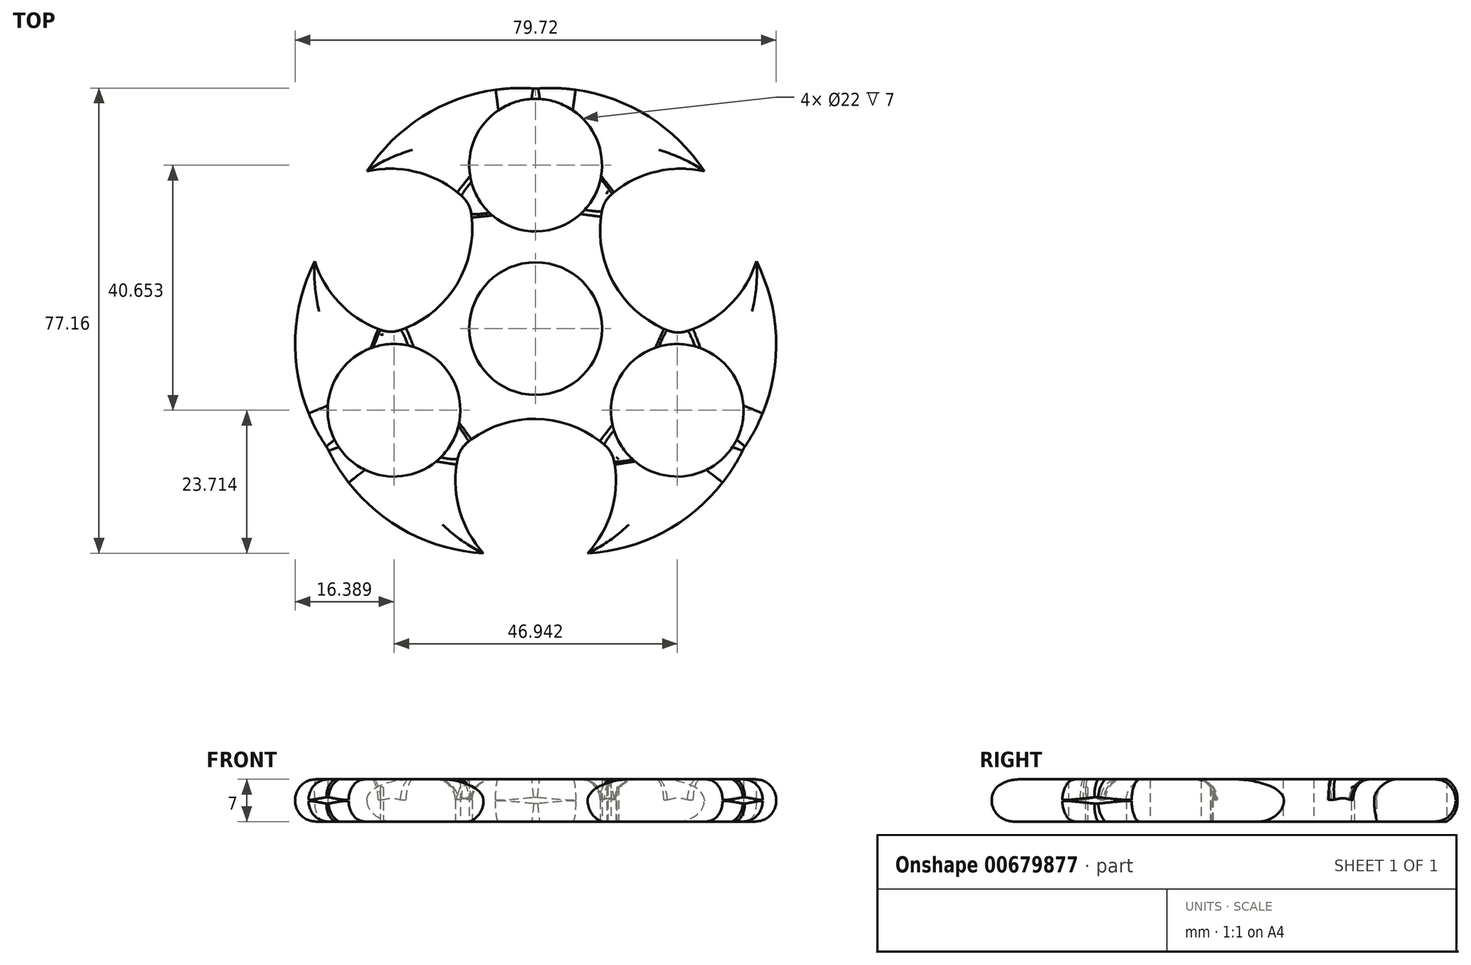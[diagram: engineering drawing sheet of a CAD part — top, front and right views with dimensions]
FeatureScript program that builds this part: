
annotation { "Feature Type Name" : "Feature", "Feature Type Description" : "" }
export const myFeature = defineFeature(function(context is Context, id is Id, definition is map)
    precondition{}
    {
        {
            var Q0;
            Q0=qCreatedBy(makeId("Top.planeOp"),FACE);
            var sketch = newSketch(context, id + "F0", { "sketchPlane" : qUnion([Q0])});
            skCircle(sketch, "E0", {"center": v(0, 40.4) * mm, "radius": 11 * mm});
            skCircle(sketch, "E1.1.0", {"center": v(-23.47, -0.25) * mm, "radius": 11 * mm});
            skCircle(sketch, "E1.2.0", {"center": v(23.47, -0.25) * mm, "radius": 11 * mm});
            skPoint(sketch, "E1.center", {"position": v(0, 13.3) * mm});
            skCircle(sketch, "E2", {"center": v(0, 13.3) * mm, "radius": 11 * mm});
            skCircle(sketch, "E3", {"center": v(0, 40.4) * mm, "radius": 12.7 * mm});
            skCircle(sketch, "E4.1.0", {"center": v(-23.47, -0.25) * mm, "radius": 12.7 * mm});
            skCircle(sketch, "E4.2.0", {"center": v(23.47, -0.25) * mm, "radius": 12.7 * mm});
            skArc(sketch, "E5", {"start": v(11.95, 36.1) * mm, "mid": v(12.48, 21.73) * mm, "end": v(23.47, 12.45) * mm});
            skArc(sketch, "E6.1.0", {"start": v(-25.72, 12.25) * mm, "mid": v(-13.54, 19.9) * mm, "end": v(-11, 34.06) * mm});
            skArc(sketch, "E6.2.0", {"start": v(13.77, -8.44) * mm, "mid": v(1.06, -1.72) * mm, "end": v(-12.47, -6.6) * mm});
            skArc(sketch, "E7", {"start": v(-11, 34.06) * mm, "mid": v(-18.76, 39) * mm, "end": v(-27.95, 39.41) * mm});
            skArc(sketch, "E8.1.0", {"start": v(-12.47, -6.6) * mm, "mid": v(-12.88, -15.8) * mm, "end": v(-8.63, -23.96) * mm});
            skArc(sketch, "E8.2.0", {"start": v(23.47, 12.45) * mm, "mid": v(31.64, 16.7) * mm, "end": v(36.59, 24.46) * mm});
            skArc(sketch, "E9", {"start": v(-35.8, -3.33) * mm, "mid": v(-25.37, -17.8) * mm, "end": v(-8.63, -23.96) * mm});
            skArc(sketch, "E10.1.0", {"start": v(32.3, -9.37) * mm, "mid": v(39.62, 6.89) * mm, "end": v(36.59, 24.46) * mm});
            skArc(sketch, "E10.2.0", {"start": v(3.49, 52.62) * mm, "mid": v(-14.25, 50.82) * mm, "end": v(-27.95, 39.41) * mm});
            skArc(sketch, "E11.MirrorCS", {"start": v(-3.49, 52.62) * mm, "mid": v(14.25, 50.82) * mm, "end": v(27.95, 39.41) * mm});
            skArc(sketch, "E12.MirrorCS", {"start": v(11, 34.06) * mm, "mid": v(18.76, 39) * mm, "end": v(27.95, 39.41) * mm});
            skArc(sketch, "E13.1.0", {"start": v(-23.47, 12.45) * mm, "mid": v(-31.64, 16.7) * mm, "end": v(-36.59, 24.46) * mm});
            skArc(sketch, "E13.1.1", {"start": v(-32.3, -9.37) * mm, "mid": v(-39.62, 6.89) * mm, "end": v(-36.59, 24.46) * mm});
            skArc(sketch, "E13.2.0", {"start": v(12.47, -6.6) * mm, "mid": v(12.88, -15.8) * mm, "end": v(8.63, -23.96) * mm});
            skArc(sketch, "E13.2.1", {"start": v(35.8, -3.33) * mm, "mid": v(25.37, -17.8) * mm, "end": v(8.63, -23.96) * mm});
            skSolve(sketch);
        }
        {
            var Q0;
            Q0=qSketchRegion(id+"F0",true);
            extrude(context, id + "F1", {"entities" : qUnion([Q0]), "depth" : 7 * mm, "offsetDistance" : 25.4 * mm});
        }
        {
            var Q0;
            Q0=makeQuery(id+"F1.opExtrude","SWEPT_EDGE",EDGE,{"disambiguationData":[OSD([sQuery(id+"F0.wireOp",EDGE,"E3"),sQuery(id+"F0.wireOp",EDGE,"E10.2.0")])]});
            var Q1;
            Q1=makeQuery(id+"F1.opExtrude","SWEPT_EDGE",EDGE,{"disambiguationData":[OSD([sQuery(id+"F0.wireOp",EDGE,"E4.1.0"),sQuery(id+"F0.wireOp",EDGE,"E9")])]});
            var Q2;
            Q2=makeQuery(id+"F1.opExtrude","SWEPT_EDGE",EDGE,{"disambiguationData":[OSD([sQuery(id+"F0.wireOp",EDGE,"E6.1.0"),sQuery(id+"F0.wireOp",EDGE,"E13.1.0")])]});
            var Q3;
            Q3=makeQuery(id+"F1.opExtrude","SWEPT_EDGE",EDGE,{"disambiguationData":[OSD([sQuery(id+"F0.wireOp",EDGE,"E4.2.0"),sQuery(id+"F0.wireOp",EDGE,"E5"),sQuery(id+"F0.wireOp",EDGE,"E8.2.0")])]});
            var Q4;
            Q4=makeQuery(id+"F1.opExtrude","SWEPT_EDGE",EDGE,{"disambiguationData":[OSD([sQuery(id+"F0.wireOp",EDGE,"E3"),sQuery(id+"F0.wireOp",EDGE,"E6.1.0"),sQuery(id+"F0.wireOp",EDGE,"E7")])]});
            var Q5;
            Q5=makeQuery(id+"F1.opExtrude","SWEPT_EDGE",EDGE,{"disambiguationData":[OSD([sQuery(id+"F0.wireOp",EDGE,"E5"),sQuery(id+"F0.wireOp",EDGE,"E12.MirrorCS")])]});
            var Q6;
            Q6=makeQuery(id+"F1.opExtrude","SWEPT_EDGE",EDGE,{"disambiguationData":[OSD([sQuery(id+"F0.wireOp",EDGE,"E4.1.0"),sQuery(id+"F0.wireOp",EDGE,"E6.2.0"),sQuery(id+"F0.wireOp",EDGE,"E8.1.0")])]});
            var Q7;
            Q7=makeQuery(id+"F1.opExtrude","SWEPT_EDGE",EDGE,{"disambiguationData":[OSD([sQuery(id+"F0.wireOp",EDGE,"E6.2.0"),sQuery(id+"F0.wireOp",EDGE,"E13.2.0")])]});
            var Q8;
            Q8=makeQuery(id+"F1.opExtrude","SWEPT_EDGE",EDGE,{"disambiguationData":[OSD([sQuery(id+"F0.wireOp",EDGE,"E4.2.0"),sQuery(id+"F0.wireOp",EDGE,"E10.1.0")])]});
            fillet(context, id + "F2", {"entities" : qUnion([Q0, Q1, Q2, Q3, Q4, Q5, Q6, Q7, Q8]), "radius" : 4.83 * mm, "tangentPropagation" : true, "rho" : 0.5, "crossSection" : FilletCrossSection.CONIC, "allowEdgeOverflow" : false});
        }
        {
            var Q0;
            Q0=makeQuery(id+"F1.opExtrude","CAP_EDGE",EDGE,{"disambiguationData":[OSD([sQuery(id+"F0.wireOp",EDGE,"E10.1.0")])],"isStart":false});
            var Q1;
            Q1=makeQuery(id+"F1.opExtrude","CAP_EDGE",EDGE,{"disambiguationData":[OSD([sQuery(id+"F0.wireOp",EDGE,"E9")])],"isStart":false});
            var Q2;
            Q2=makeQuery(id+"F1.opExtrude","CAP_EDGE",EDGE,{"disambiguationData":[OSD([sQuery(id+"F0.wireOp",EDGE,"E10.2.0")])],"isStart":false});
            var Q3;
            Q3=makeQuery(id+"F1.opExtrude","CAP_EDGE",EDGE,{"disambiguationData":[OSD([sQuery(id+"F0.wireOp",EDGE,"E9")])],"isStart":true});
            var Q4;
            Q4=makeQuery(id+"F1.opExtrude","CAP_EDGE",EDGE,{"disambiguationData":[OSD([sQuery(id+"F0.wireOp",EDGE,"E10.1.0")])],"isStart":true});
            var Q5;
            Q5=makeQuery(id+"F1.opExtrude","CAP_EDGE",EDGE,{"disambiguationData":[OSD([sQuery(id+"F0.wireOp",EDGE,"E10.2.0")])],"isStart":true});
            var Q6;
            Q6=makeQuery(id+"F1.opExtrude","CAP_EDGE",EDGE,{"disambiguationData":[OSD([sQuery(id+"F0.wireOp",EDGE,"E8.2.0")])],"isStart":false});
            var Q7;
            {var subQ0=sQuery(id+"F0.wireOp",EDGE,"E5");Q7=makeQuery(id+"F1.opExtrude","CAP_EDGE",EDGE,{"disambiguationData":[OSD([subQ0]),TDD([makeQuery(id+"F0.imprint","IMPRINT",EDGE,{"disambiguationData":[TD([[makeQuery(id+"F0.imprint","INTERSECT",VERTEX,{"derivedFrom":[subQ0,sQuery(id+"F0.wireOp",EDGE,"E12.MirrorCS")]}),-1.0]])],"derivedFrom":subQ0})])],"isStart":false});}
            var Q8;
            {var subQ0=sQuery(id+"F0.wireOp",EDGE,"E6.2.0");Q8=makeQuery(id+"F1.opExtrude","CAP_EDGE",EDGE,{"disambiguationData":[OSD([subQ0]),TDD([makeQuery(id+"F0.imprint","IMPRINT",EDGE,{"disambiguationData":[TD([[makeQuery(id+"F0.imprint","INTERSECT",VERTEX,{"derivedFrom":[subQ0,sQuery(id+"F0.wireOp",EDGE,"E13.2.0")]}),-1.0]])],"derivedFrom":subQ0})])],"isStart":false});}
            var Q9;
            {var subQ0=sQuery(id+"F0.wireOp",EDGE,"E6.1.0");Q9=makeQuery(id+"F1.opExtrude","CAP_EDGE",EDGE,{"disambiguationData":[OSD([subQ0]),TDD([makeQuery(id+"F0.imprint","IMPRINT",EDGE,{"disambiguationData":[TD([[makeQuery(id+"F0.imprint","INTERSECT",VERTEX,{"derivedFrom":[subQ0,sQuery(id+"F0.wireOp",EDGE,"E13.1.0")]}),-1.0]])],"derivedFrom":subQ0})])],"isStart":false});}
            fillet(context, id + "F3", {"entities" : qUnion([Q0, Q1, Q2, Q3, Q4, Q5, Q6, Q7, Q8, Q9]), "radius" : 3.43 * mm, "tangentPropagation" : true, "allowEdgeOverflow" : false});
        }
    });
